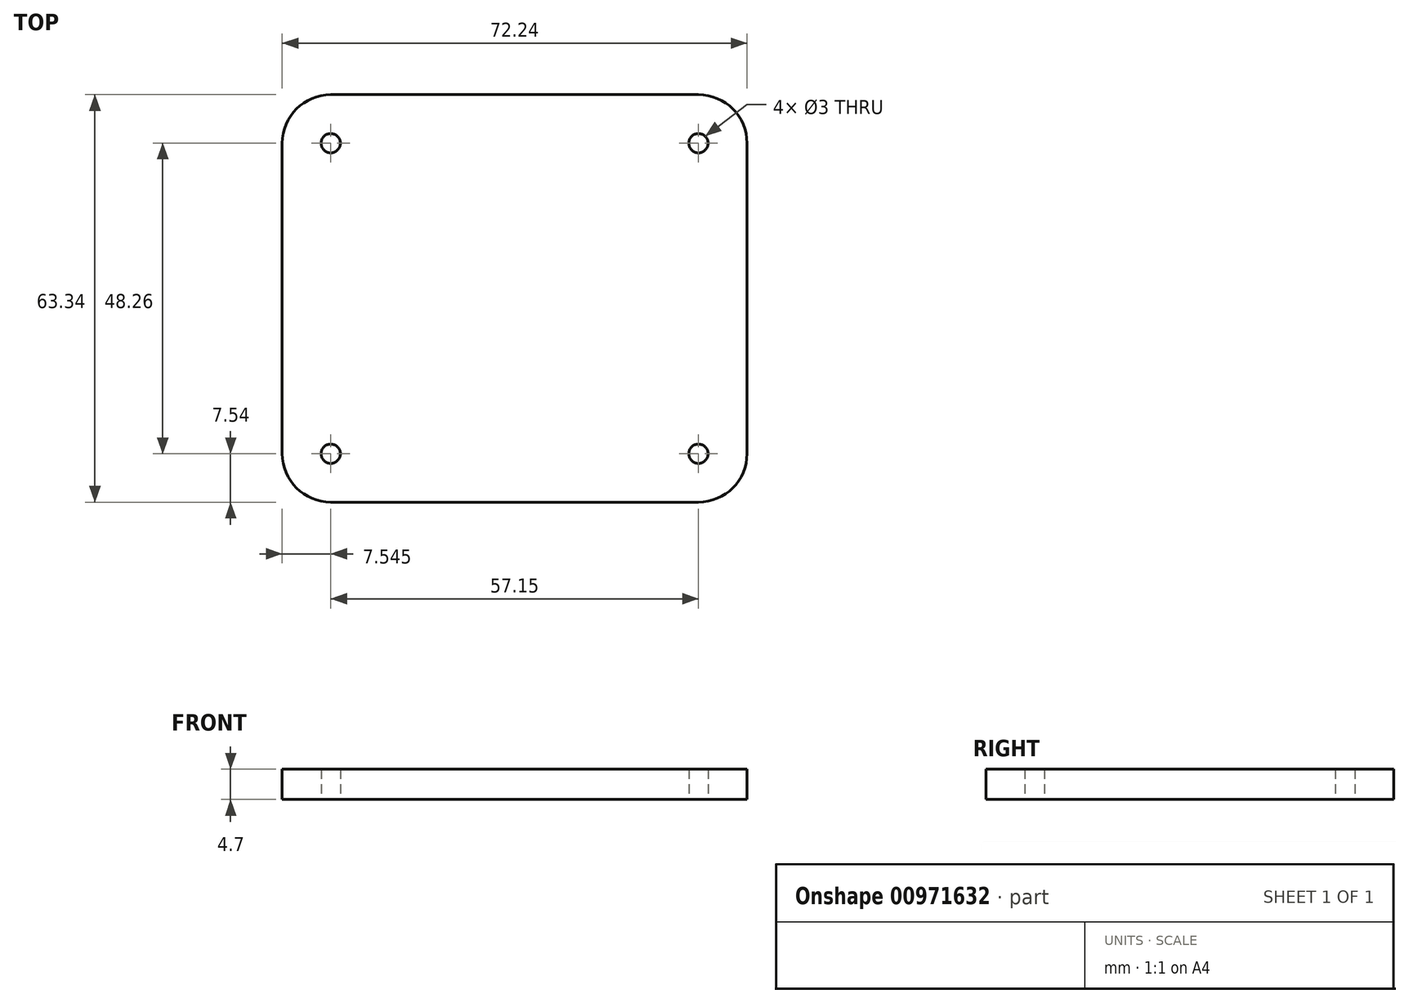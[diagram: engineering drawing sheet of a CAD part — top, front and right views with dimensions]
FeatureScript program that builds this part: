
annotation { "Feature Type Name" : "Feature", "Feature Type Description" : "" }
export const myFeature = defineFeature(function(context is Context, id is Id, definition is map)
    precondition{}
    {
        {
            var Q0;
            Q0=qCreatedBy(makeId("Top.planeOp"),FACE);
            var sketch = newSketch(context, id + "F0", { "sketchPlane" : qUnion([Q0])});
            skLineSegment(sketch, "E0.bottom", {"start": v(-28.57, 31.67) * mm, "end": v(28.58, 31.67) * mm});
            skLineSegment(sketch, "E0.top", {"start": v(-28.57, -31.67) * mm, "end": v(28.57, -31.67) * mm});
            skLineSegment(sketch, "E0.left", {"start": v(-36.11, 24.13) * mm, "end": v(-36.12, -24.13) * mm});
            skLineSegment(sketch, "E0.right", {"start": v(36.12, 24.13) * mm, "end": v(36.11, -24.13) * mm});
            skPoint(sketch, "E0.middle", {"position": v(0, 0) * mm});
            skPoint(sketch, "E1.visualSharp", {"position": v(-36.11, 31.67) * mm});
            skArc(sketch, "E1.filletArc", {"start": v(-28.57, 31.67) * mm, "mid": v(-33.9, 29.46) * mm, "end": v(-36.11, 24.13) * mm});
            skPoint(sketch, "E2.visualSharp", {"position": v(36.12, 31.67) * mm});
            skArc(sketch, "E2.filletArc", {"start": v(36.12, 24.13) * mm, "mid": v(33.9, 29.46) * mm, "end": v(28.58, 31.67) * mm});
            skPoint(sketch, "E3.visualSharp", {"position": v(36.11, -31.67) * mm});
            skArc(sketch, "E3.filletArc", {"start": v(28.57, -31.67) * mm, "mid": v(33.9, -29.46) * mm, "end": v(36.11, -24.13) * mm});
            skPoint(sketch, "E4.visualSharp", {"position": v(-36.11, -31.67) * mm});
            skArc(sketch, "E4.filletArc", {"start": v(-36.11, -24.13) * mm, "mid": v(-33.9, -29.46) * mm, "end": v(-28.57, -31.67) * mm});
            skCircle(sketch, "E5", {"center": v(-28.57, 24.13) * mm, "radius": 1.5 * mm});
            skLineSegment(sketch, "E6", {"start": v(0, 31.67) * mm, "end": v(0, -31.67) * mm, "construction": true});
            skLineSegment(sketch, "E7", {"start": v(-36.12, 0) * mm, "end": v(36.12, 0) * mm, "construction": true});
            skCircle(sketch, "E8.MirrorC", {"center": v(28.58, 24.13) * mm, "radius": 1.5 * mm});
            skCircle(sketch, "E9.MirrorC", {"center": v(28.58, -24.13) * mm, "radius": 1.5 * mm});
            skCircle(sketch, "E10.MirrorC", {"center": v(-28.57, -24.13) * mm, "radius": 1.5 * mm});
            skSolve(sketch);
        }
        {
            var Q0;
            Q0=makeQuery(id+"F0.imprint","IMPRINT",FACE,{"disambiguationData":[TD([[makeQuery(id+"F0.imprint","IMPRINT",EDGE,{"derivedFrom":sQuery(id+"F0.wireOp",EDGE,"E0.bottom")}),-1.0]])]});
            extrude(context, id + "F1", {"entities" : qUnion([Q0]), "depth" : 4.7 * mm, "offsetDistance" : 25 * mm});
        }
    });
